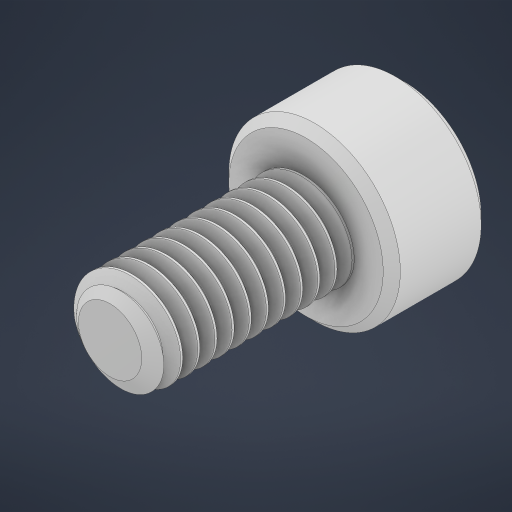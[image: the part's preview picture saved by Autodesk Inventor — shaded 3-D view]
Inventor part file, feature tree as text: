
AUTODESK INVENTOR PART (.ipt)
format: ipt  version: 2023 (Build 270158000, 158)  size: 619,008 bytes
history: native  units: in
note: dims shown in document units (in); Inventor stores cm internally (conversion verified against a paired STEP export)
features: chamfer x1
ambient origin geometry x8: Origin, YZ Plane, XZ Plane, XY Plane, X Axis, Y Axis, Z Axis, Center Point
bodies: Solid1 (feature_tree)
feature tree (1):
  chamfer  "Chamfer1"  [1 undecoded]
note: 1 required parameter value undecoded (feature->parameter linkage not recoverable at this tier; creation-order binding heuristic only, values carry confidence <= 0.55)
